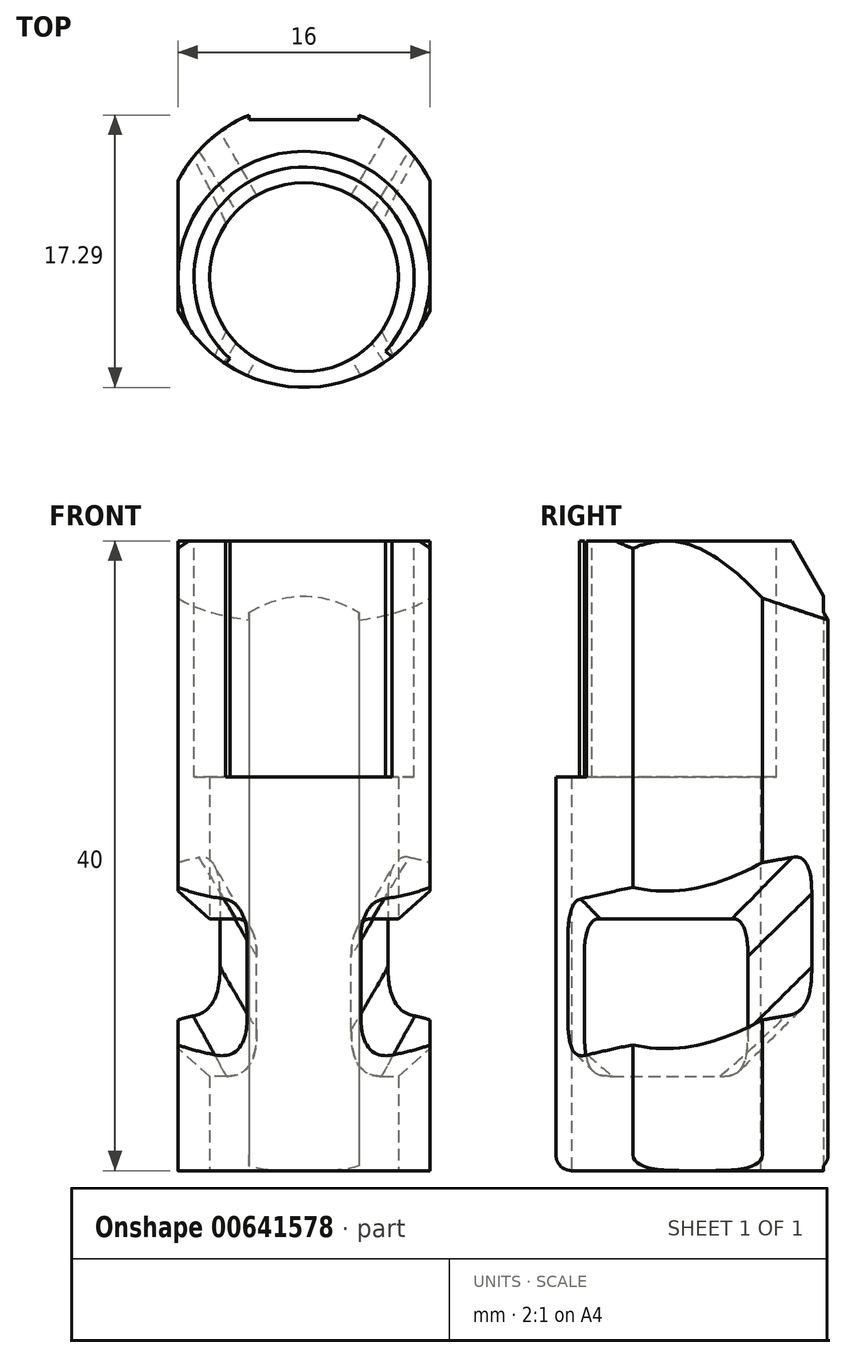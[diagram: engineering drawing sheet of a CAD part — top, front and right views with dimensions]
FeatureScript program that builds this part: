
annotation { "Feature Type Name" : "Feature", "Feature Type Description" : "" }
export const myFeature = defineFeature(function(context is Context, id is Id, definition is map)
    precondition{}
    {
        {
            var Q0;
            Q0=qCreatedBy(makeId("Top.planeOp"),FACE);
            var sketch = newSketch(context, id + "F0", { "sketchPlane" : qUnion([Q0])});
            skCircle(sketch, "E0", {"center": v(0, 0) * mm, "radius": 6 * mm});
            skArc(sketch, "E1", {"start": v(-8, -2.12) * mm, "mid": v(0, -7) * mm, "end": v(8, -2.12) * mm});
            skLineSegment(sketch, "E2.left", {"start": v(8, -2.12) * mm, "end": v(8, 6.12) * mm});
            skLineSegment(sketch, "E2.right", {"start": v(-8, -2.12) * mm, "end": v(-8, 6.12) * mm});
            skPoint(sketch, "E3.orphan", {"position": v(-8, 13.3) * mm});
            skPoint(sketch, "E2.bottom.end.orphan", {"position": v(-8, -13.3) * mm});
            skPoint(sketch, "E4.orphan", {"position": v(8, -13.3) * mm});
            skPoint(sketch, "E5.orphan", {"position": v(8, 13.3) * mm});
            skArc(sketch, "E6.trimOffspring", {"start": v(8, 6.12) * mm, "mid": v(6.12, 8.6) * mm, "end": v(3.5, 10.3) * mm});
            skLineSegment(sketch, "E7.bottom", {"start": v(3.5, 10) * mm, "end": v(-3.5, 10) * mm});
            skLineSegment(sketch, "E7.left", {"start": v(3.5, 10) * mm, "end": v(3.5, 10.3) * mm});
            skLineSegment(sketch, "E7.right", {"start": v(-3.5, 10) * mm, "end": v(-3.5, 10.3) * mm});
            skPoint(sketch, "E7.middle", {"position": v(0, 11) * mm});
            skPoint(sketch, "E8.orphan", {"position": v(3.5, 12) * mm});
            skArc(sketch, "E9.trimOffspring", {"start": v(-3.5, 10.3) * mm, "mid": v(-6.12, 8.6) * mm, "end": v(-8, 6.12) * mm});
            skPoint(sketch, "E10.orphan", {"position": v(-3.5, 12) * mm});
            skSolve(sketch);
        }
        {
            var Q0;
            Q0=makeQuery(id+"F0.imprint","IMPRINT",FACE,{"disambiguationData":[TD([[makeQuery(id+"F0.imprint","IMPRINT",EDGE,{"derivedFrom":sQuery(id+"F0.wireOp",EDGE,"E0")}),-1.0]])]});
            extrude(context, id + "F1", {"entities" : qUnion([Q0]), "depth" : 40 * mm, "offsetDistance" : 25 * mm});
        }
        {
            var Q0;
            Q0=makeQuery(id+"F1.opExtrude","CAP_EDGE",EDGE,{"disambiguationData":[OSD([sQuery(id+"F0.wireOp",EDGE,"E9.trimOffspring")])],"isStart":true});
            var Q1;
            Q1=makeQuery(id+"F1.opExtrude","CAP_EDGE",EDGE,{"disambiguationData":[OSD([sQuery(id+"F0.wireOp",EDGE,"E6.trimOffspring")])],"isStart":true});
            var Q2;
            Q2=makeQuery(id+"F1.opExtrude","CAP_EDGE",EDGE,{"disambiguationData":[OSD([sQuery(id+"F0.wireOp",EDGE,"E1")])],"isStart":true});
            fillet(context, id + "F2", {"entities" : qUnion([Q0, Q1, Q2]), "tangentPropagation" : true, "radius" : 1 * mm, "defaultsChanged" : true, "vertexSettings" : [], "allowEdgeOverflow" : false});
        }
        {
            var Q0;
            Q0=makeQuery(id+"F1.opExtrude","CAP_FACE",FACE,{"disambiguationData":[OSD([sQuery(id+"F0.wireOp",EDGE,"E0"),sQuery(id+"F0.wireOp",EDGE,"E1"),sQuery(id+"F0.wireOp",EDGE,"E2.left"),sQuery(id+"F0.wireOp",EDGE,"E2.right"),sQuery(id+"F0.wireOp",EDGE,"E6.trimOffspring"),sQuery(id+"F0.wireOp",EDGE,"E7.bottom"),sQuery(id+"F0.wireOp",EDGE,"E7.left"),sQuery(id+"F0.wireOp",EDGE,"E7.right"),sQuery(id+"F0.wireOp",EDGE,"E9.trimOffspring")])],"isStart":false});
            var sketch = newSketch(context, id + "F3", { "sketchPlane" : qUnion([Q0])});
            skCircle(sketch, "E11", {"center": v(0, 0) * mm, "radius": 7 * mm});
            skLineSegment(sketch, "E12", {"start": v(0, 0) * mm, "end": v(-4.99, -5.5) * mm});
            skLineSegment(sketch, "E13", {"start": v(0, 0) * mm, "end": v(5.58, -5.06) * mm});
            skLineSegment(sketch, "E14", {"start": v(0, 0) * mm, "end": v(0, -8.98) * mm, "construction": true});
            skSolve(sketch);
        }
        {
            var Q0;
            {var subQ0=sQuery(id+"F3.wireOp",EDGE,"E12");var subQ1=sQuery(id+"F3.wireOp",EDGE,"E11");var subQ2=makeQuery(id+"F3.imprint","INTERSECT",VERTEX,{"derivedFrom":[subQ1,subQ0]});Q0=makeQuery(id+"F3.imprint","IMPRINT",FACE,{"disambiguationData":[TD([[makeQuery(id+"F3.imprint","IMPRINT",EDGE,{"disambiguationData":[TD([[subQ2,1.0]])],"derivedFrom":subQ1}),1.0]])]});}
            var Q1;
            {var subQ1=sQuery(id+"F3.wireOp",EDGE,"E11");var subQ5=sQuery(id+"F3.wireOp",EDGE,"E12");var subQ6=makeQuery(id+"F3.imprint","INTERSECT",VERTEX,{"derivedFrom":[subQ1,subQ5]});Q1=makeQuery(id+"F3.imprint","IMPRINT",FACE,{"disambiguationData":[TD([[makeQuery(id+"F3.imprint","IMPRINT",EDGE,{"disambiguationData":[TD([[subQ6,-1.0]])],"derivedFrom":subQ1}),1.0]])]});}
            var Q2;
            {var subQ0=sQuery(id+"F3.wireOp",EDGE,"E12");var subQ1=sQuery(id+"F3.wireOp",EDGE,"E11");var subQ2=makeQuery(id+"F3.imprint","INTERSECT",VERTEX,{"derivedFrom":[subQ1,subQ0]});Q2=makeQuery(id+"F3.imprint","IMPRINT",FACE,{"disambiguationData":[TD([[makeQuery(id+"F3.imprint","IMPRINT",EDGE,{"disambiguationData":[TD([[subQ2,-1.0]])],"derivedFrom":subQ1}),-1.0]])]});}
            var Q3;
            {var subQ0=sQuery(id+"F3.wireOp",EDGE,"E13");var subQ1=sQuery(id+"F3.wireOp",EDGE,"E11");var subQ2=makeQuery(id+"F3.imprint","INTERSECT",VERTEX,{"derivedFrom":[subQ1,subQ0]});Q3=makeQuery(id+"F3.imprint","IMPRINT",FACE,{"disambiguationData":[TD([[makeQuery(id+"F3.imprint","IMPRINT",EDGE,{"disambiguationData":[TD([[subQ2,1.0]])],"derivedFrom":subQ1}),-1.0]])]});}
            extrude(context, id + "F4", {"entities" : qUnion([Q0, Q1, Q2, Q3]), "operationType" : NewBodyOperationType.REMOVE, "oppositeDirection" : true, "depth" : 15 * mm, "offsetDistance" : 25 * mm});
        }
        {
            var Q0;
            Q0=qCreatedBy(makeId("Front.planeOp"),FACE);
            var sketch = newSketch(context, id + "F5", { "sketchPlane" : qUnion([Q0])});
            skLineSegment(sketch, "E15", {"start": v(0, 0) * mm, "end": v(0, 54) * mm, "construction": true});
            skPoint(sketch, "E16.0", {"position": v(-8, 40) * mm});
            skPoint(sketch, "E17.0", {"position": v(8, 40) * mm});
            skLineSegment(sketch, "E18", {"start": v(0, 54) * mm, "end": v(-12.53, 32.08) * mm});
            skLineSegment(sketch, "E19", {"start": v(0, 55.85) * mm, "end": v(0, 54) * mm});
            skLineSegment(sketch, "E20", {"start": v(-12.53, 32.08) * mm, "end": v(-12.53, 55.85) * mm});
            skLineSegment(sketch, "E21", {"start": v(-12.53, 55.85) * mm, "end": v(0, 55.85) * mm});
            skSolve(sketch);
        }
        {
            var Q0;
            Q0=makeQuery(id+"F5.imprint","IMPRINT",FACE,{"disambiguationData":[TD([[makeQuery(id+"F5.imprint","IMPRINT",EDGE,{"derivedFrom":sQuery(id+"F5.wireOp",EDGE,"E18")}),-1.0]])]});
            var Q1;
            Q1=sQuery(id+"F5.wireOp",EDGE,"E15");
            revolve(context, id + "F6", {"operationType" : NewBodyOperationType.REMOVE, "surfaceOperationType" : NewSurfaceOperationType.NEW, "entities" : qUnion([Q0]), "axis" : qUnion([Q1]), "revolveType" : RevolveType.FULL});
        }
        {
            var Q0;
            Q0=qCreatedBy(makeId("Front.planeOp"),FACE);
            var sketch = newSketch(context, id + "F7", { "sketchPlane" : qUnion([Q0])});
            skLineSegment(sketch, "E22.0.0", {"start": v(-3.5, 0.32) * mm, "end": v(-3.5, 35.46) * mm});
            skFitSpline(sketch, "E22.0.1", {"points": [v(-3.5, 35.46) * mm, v(-3.23, 35.61) * mm, v(-2.68, 35.9) * mm, v(-1.96, 36.18) * mm, v(-1.37, 36.34) * mm, v(-0.92, 36.43) * mm, v(-0.45, 36.49) * mm, v(0.16, 36.51) * mm, v(0.92, 36.45) * mm, v(1.83, 36.23) * mm, v(2.69, 35.9) * mm, v(3.23, 35.61) * mm, v(3.5, 35.46) * mm]});
            skLineSegment(sketch, "E22.0.2", {"start": v(3.5, 35.46) * mm, "end": v(3.5, 0.32) * mm});
            skFitSpline(sketch, "E22.0.3", {"points": [v(3.5, 0.32) * mm, v(3.36, 0.26) * mm, v(3.08, 0.17) * mm, v(2.5, 0.06) * mm, v(1.77, 0) * mm, v(0.88, 0) * mm, v(0.3, 0) * mm, v(0, 0) * mm]});
            skFitSpline(sketch, "E22.0.4", {"points": [v(0, 0) * mm, v(-0.3, 0) * mm, v(-0.88, 0) * mm, v(-1.77, 0.01) * mm, v(-2.5, 0.06) * mm, v(-3.08, 0.17) * mm, v(-3.36, 0.26) * mm, v(-3.5, 0.32) * mm]});
            skLineSegment(sketch, "E23.left", {"start": v(0, 6) * mm, "end": v(0, 16) * mm});
            skLineSegment(sketch, "E23.right", {"start": v(6, 6) * mm, "end": v(6, 16) * mm});
            skLineSegment(sketch, "E24", {"start": v(6, 16) * mm, "end": v(12.22, 21.46) * mm});
            skLineSegment(sketch, "E25", {"start": v(12.22, 21.46) * mm, "end": v(12.22, 11.46) * mm});
            skLineSegment(sketch, "E26", {"start": v(12.22, 11.46) * mm, "end": v(6, 6) * mm});
            skLineSegment(sketch, "E27.MirrorCS", {"start": v(-12.22, 11.46) * mm, "end": v(-6, 6) * mm});
            skLineSegment(sketch, "E28.MirrorCS", {"start": v(-12.22, 21.46) * mm, "end": v(-12.22, 11.46) * mm});
            skLineSegment(sketch, "E29.MirrorCS", {"start": v(-6, 6) * mm, "end": v(-6, 16) * mm});
            skLineSegment(sketch, "E30.MirrorCS", {"start": v(-6, 16) * mm, "end": v(-12.22, 21.46) * mm});
            skSolve(sketch);
        }
        {
            var Q0;
            Q0=makeQuery(id+"F7.imprint","IMPRINT",FACE,{"disambiguationData":[TD([[makeQuery(id+"F7.imprint","IMPRINT",EDGE,{"derivedFrom":sQuery(id+"F7.wireOp",EDGE,"E23.right")}),-1.0]])]});
            var Q1;
            Q1=makeQuery(id+"F7.imprint","IMPRINT",FACE,{"disambiguationData":[TD([[makeQuery(id+"F7.imprint","IMPRINT",EDGE,{"derivedFrom":sQuery(id+"F7.wireOp",EDGE,"E27.MirrorCS")}),1.0]])]});
            var Q2;
            Q2=sQuery(id+"F7.wireOp",EDGE,"E23.left");
            revolve(context, id + "F8", {"operationType" : NewBodyOperationType.REMOVE, "surfaceOperationType" : NewSurfaceOperationType.NEW, "entities" : qUnion([Q0, Q1]), "axis" : qUnion([Q2]), "revolveType" : RevolveType.TWO_DIRECTIONS, "angle" : 60 * degree, "angleBack" : 300 * degree});
        }
        {
            var Q0;
            Q0=makeQuery(id+"F8.boolean.opBoolean","COPY",EDGE,{"derivedFrom":makeQuery(id+"F8.opRevolve","CAP_EDGE",EDGE,{"disambiguationData":[OSD([sQuery(id+"F7.wireOp",EDGE,"E26")])],"isStart":false})});
            var Q1;
            Q1=makeQuery(id+"F8.boolean.opBoolean","COPY",EDGE,{"derivedFrom":makeQuery(id+"F8.opRevolve","CAP_EDGE",EDGE,{"disambiguationData":[OSD([sQuery(id+"F7.wireOp",EDGE,"E24")])],"isStart":false})});
            var Q2;
            Q2=makeQuery(id+"F8.boolean.opBoolean","COPY",EDGE,{"derivedFrom":makeQuery(id+"F8.opRevolve","CAP_EDGE",EDGE,{"disambiguationData":[OSD([sQuery(id+"F7.wireOp",EDGE,"E24")])],"isStart":true})});
            var Q3;
            Q3=makeQuery(id+"F8.boolean.opBoolean","COPY",EDGE,{"derivedFrom":makeQuery(id+"F8.opRevolve","CAP_EDGE",EDGE,{"disambiguationData":[OSD([sQuery(id+"F7.wireOp",EDGE,"E26")])],"isStart":true})});
            var Q4;
            Q4=makeQuery(id+"F8.boolean.opBoolean","COPY",EDGE,{"derivedFrom":makeQuery(id+"F8.opRevolve","CAP_EDGE",EDGE,{"disambiguationData":[OSD([sQuery(id+"F7.wireOp",EDGE,"E27.MirrorCS")])],"isStart":false})});
            var Q5;
            Q5=makeQuery(id+"F8.boolean.opBoolean","COPY",EDGE,{"derivedFrom":makeQuery(id+"F8.opRevolve","CAP_EDGE",EDGE,{"disambiguationData":[OSD([sQuery(id+"F7.wireOp",EDGE,"E27.MirrorCS")])],"isStart":true})});
            var Q6;
            Q6=makeQuery(id+"F8.boolean.opBoolean","COPY",EDGE,{"derivedFrom":makeQuery(id+"F8.opRevolve","CAP_EDGE",EDGE,{"disambiguationData":[OSD([sQuery(id+"F7.wireOp",EDGE,"E30.MirrorCS")])],"isStart":true})});
            var Q7;
            Q7=makeQuery(id+"F8.boolean.opBoolean","COPY",EDGE,{"derivedFrom":makeQuery(id+"F8.opRevolve","CAP_EDGE",EDGE,{"disambiguationData":[OSD([sQuery(id+"F7.wireOp",EDGE,"E30.MirrorCS")])],"isStart":false})});
            fillet(context, id + "F9", {"entities" : qUnion([Q0, Q1, Q2, Q3, Q4, Q5, Q6, Q7]), "tangentPropagation" : true, "crossSection" : FilletCrossSection.CURVATURE, "radius" : 2 * mm, "magnitude" : 0.5, "defaultsChanged" : false, "vertexSettings" : []});
        }
    });
